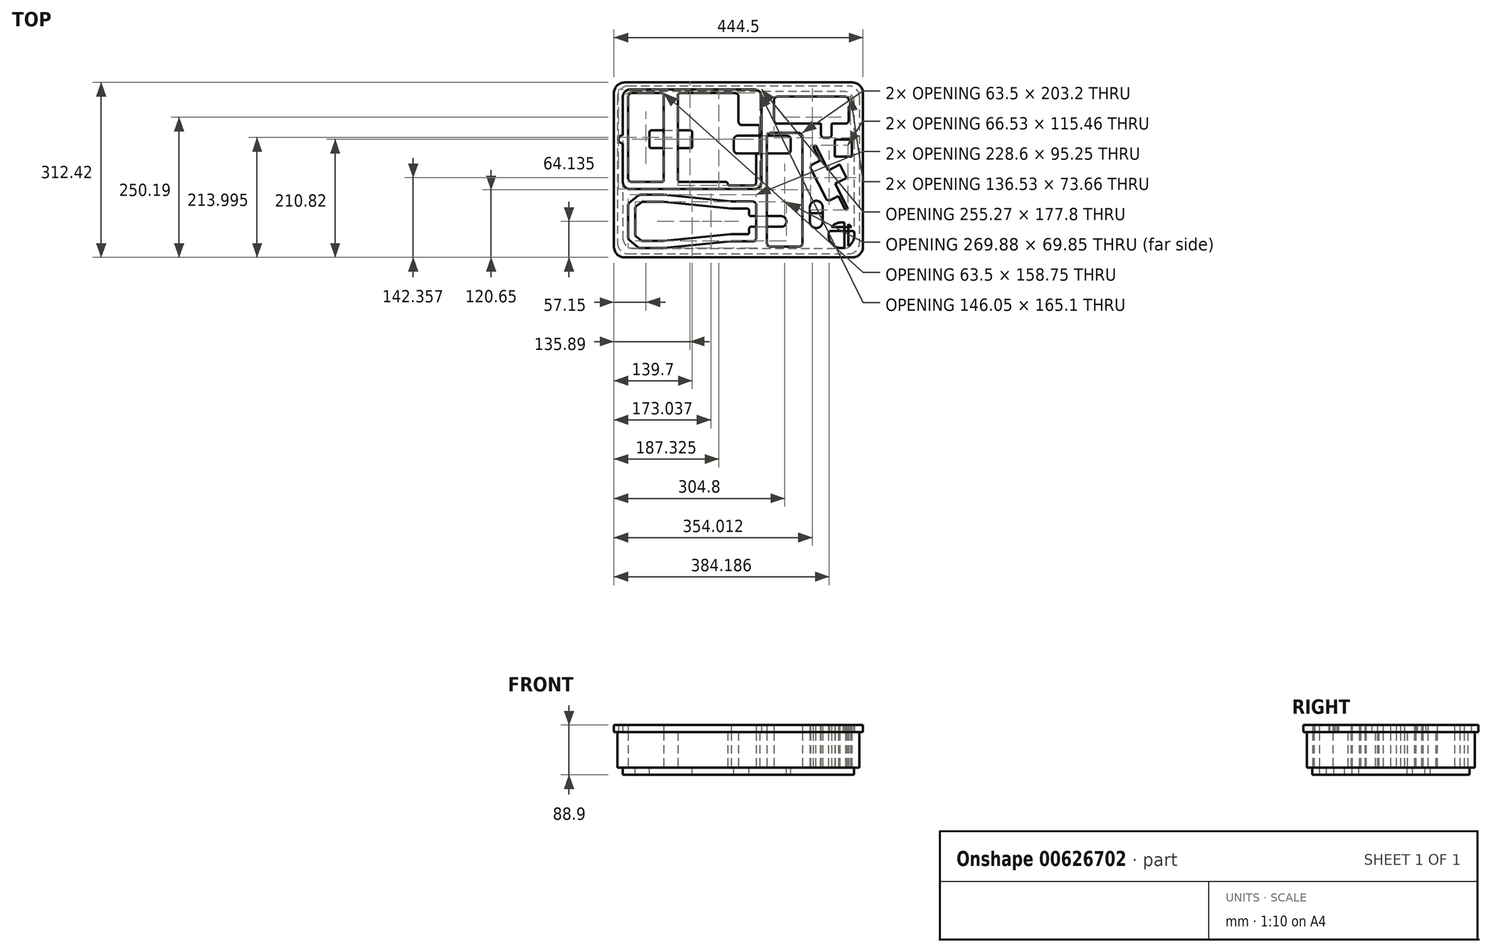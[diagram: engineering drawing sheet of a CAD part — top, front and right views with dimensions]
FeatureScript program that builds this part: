
annotation { "Feature Type Name" : "Feature", "Feature Type Description" : "" }
export const myFeature = defineFeature(function(context is Context, id is Id, definition is map)
    precondition{}
    {
        {
            var Q0;
            Q0=qCreatedBy(makeId("Top.planeOp"),FACE);
            var sketch = newSketch(context, id + "F0", { "sketchPlane" : qUnion([Q0])});
            skLineSegment(sketch, "E0.bottom", {"start": v(-196.85, 149.86) * mm, "end": v(196.85, 149.86) * mm});
            skLineSegment(sketch, "E0.top", {"start": v(-196.85, -149.86) * mm, "end": v(196.85, -149.86) * mm});
            skLineSegment(sketch, "E0.left", {"start": v(-215.9, 130.81) * mm, "end": v(-215.9, -130.81) * mm});
            skLineSegment(sketch, "E0.right", {"start": v(215.9, 130.81) * mm, "end": v(215.9, -130.8) * mm});
            skLineSegment(sketch, "E1.bottom", {"start": v(-196.85, -15.24) * mm, "end": v(-196.85, 130.81) * mm});
            skLineSegment(sketch, "E1.top", {"start": v(31.75, -21.59) * mm, "end": v(31.75, 26.04) * mm});
            skLineSegment(sketch, "E1.right", {"start": v(-190.5, 137.16) * mm, "end": v(-136.52, 137.16) * mm});
            skLineSegment(sketch, "E2.bottom", {"start": v(171.94, 54.19) * mm, "end": v(202.42, 54.19) * mm});
            skLineSegment(sketch, "E2.top", {"start": v(171.94, 23.7) * mm, "end": v(202.42, 23.7) * mm});
            skLineSegment(sketch, "E2.left", {"start": v(171.94, 54.19) * mm, "end": v(171.94, 23.7) * mm});
            skLineSegment(sketch, "E2.right", {"start": v(202.42, 54.19) * mm, "end": v(202.42, 23.7) * mm});
            skLineSegment(sketch, "E3", {"start": v(142.6, -24.8) * mm, "end": v(186.74, -2.32) * mm, "construction": true});
            skLineSegment(sketch, "E4", {"start": v(142.6, -24.8) * mm, "end": v(155.87, -50.83) * mm});
            skLineSegment(sketch, "E5", {"start": v(164.4, -53.6) * mm, "end": v(177.99, -46.7) * mm});
            skLineSegment(sketch, "E6", {"start": v(177.99, -46.7) * mm, "end": v(190.67, -71.59) * mm});
            skLineSegment(sketch, "E7", {"start": v(190.67, -71.59) * mm, "end": v(195.2, -69.28) * mm});
            skLineSegment(sketch, "E8", {"start": v(160.32, -0.82) * mm, "end": v(180.68, 9.56) * mm});
            skLineSegment(sketch, "E9", {"start": v(180.68, 9.56) * mm, "end": v(186.74, -2.32) * mm});
            skPoint(sketch, "E10.visualSharp", {"position": v(158.75, -56.5) * mm});
            skArc(sketch, "E10.filletArc", {"start": v(155.87, -50.83) * mm, "mid": v(159.56, -54) * mm, "end": v(164.4, -53.6) * mm});
            skArc(sketch, "E11.MirrorCS", {"start": v(129.35, 1.22) * mm, "mid": v(128.96, 6.06) * mm, "end": v(132.12, 9.76) * mm});
            skLineSegment(sketch, "E12.MirrorCS", {"start": v(145.7, 16.68) * mm, "end": v(133.02, 41.57) * mm});
            skLineSegment(sketch, "E13.MirrorCS", {"start": v(132.12, 9.76) * mm, "end": v(145.7, 16.68) * mm});
            skPoint(sketch, "E14.MirrorP", {"position": v(126.46, 6.88) * mm});
            skLineSegment(sketch, "E15.MirrorCS", {"start": v(172.42, -24.58) * mm, "end": v(192.8, -14.2) * mm});
            skLineSegment(sketch, "E16.MirrorCS", {"start": v(142.6, -24.8) * mm, "end": v(129.35, 1.22) * mm});
            skLineSegment(sketch, "E17.MirrorCS", {"start": v(192.8, -14.2) * mm, "end": v(186.74, -2.32) * mm});
            skLineSegment(sketch, "E18", {"start": v(172.42, -24.58) * mm, "end": v(195.2, -69.28) * mm});
            skPoint(sketch, "E19.visualSharp", {"position": v(-215.9, 149.86) * mm});
            skArc(sketch, "E19.filletArc", {"start": v(-196.85, 149.86) * mm, "mid": v(-210.32, 144.28) * mm, "end": v(-215.9, 130.81) * mm});
            skPoint(sketch, "E20.visualSharp", {"position": v(215.9, 149.86) * mm});
            skArc(sketch, "E20.filletArc", {"start": v(215.9, 130.81) * mm, "mid": v(210.32, 144.28) * mm, "end": v(196.85, 149.86) * mm});
            skPoint(sketch, "E21.visualSharp", {"position": v(215.9, -149.86) * mm});
            skArc(sketch, "E21.filletArc", {"start": v(196.85, -149.86) * mm, "mid": v(210.32, -144.28) * mm, "end": v(215.9, -130.8) * mm});
            skPoint(sketch, "E22.visualSharp", {"position": v(-215.9, -149.86) * mm});
            skArc(sketch, "E22.filletArc", {"start": v(-215.9, -130.81) * mm, "mid": v(-210.32, -144.28) * mm, "end": v(-196.85, -149.86) * mm});
            skPoint(sketch, "E23.visualSharp", {"position": v(-196.85, -27.94) * mm});
            skPoint(sketch, "E24.visualSharp", {"position": v(31.75, -27.94) * mm});
            skArc(sketch, "E24.filletArc", {"start": v(25.4, -27.94) * mm, "mid": v(29.9, -26.08) * mm, "end": v(31.75, -21.59) * mm});
            skPoint(sketch, "E25.visualSharp", {"position": v(-196.85, 137.16) * mm});
            skArc(sketch, "E25.filletArc", {"start": v(-190.5, 137.16) * mm, "mid": v(-195, 135.3) * mm, "end": v(-196.85, 130.81) * mm});
            skPoint(sketch, "E26.visualSharp", {"position": v(31.75, 137.16) * mm});
            skArc(sketch, "E26.filletArc", {"start": v(31.75, 130.81) * mm, "mid": v(29.9, 135.3) * mm, "end": v(25.4, 137.16) * mm, "construction": true});
            skLineSegment(sketch, "E27.bottom", {"start": v(63.5, 88.9) * mm, "end": v(63.5, 124.46) * mm});
            skLineSegment(sketch, "E27.top", {"start": v(196.85, 88.9) * mm, "end": v(196.85, 112.08) * mm});
            skLineSegment(sketch, "E27.left", {"start": v(69.85, 82.55) * mm, "end": v(146.05, 82.55) * mm});
            skLineSegment(sketch, "E27.right", {"start": v(69.85, 130.81) * mm, "end": v(190.5, 130.81) * mm});
            skLineSegment(sketch, "E28.bottom", {"start": v(147.32, 81.28) * mm, "end": v(147.32, 63.5) * mm});
            skLineSegment(sketch, "E28.top", {"start": v(166.37, 81.28) * mm, "end": v(166.37, 63.5) * mm});
            skLineSegment(sketch, "E28.right", {"start": v(153.67, 57.15) * mm, "end": v(160.02, 57.15) * mm});
            skLineSegment(sketch, "E29.trimOffspring", {"start": v(167.64, 82.55) * mm, "end": v(190.5, 82.55) * mm});
            skLineSegment(sketch, "E30", {"start": v(147.32, 82.55) * mm, "end": v(166.37, 82.55) * mm, "construction": true});
            skPoint(sketch, "E31.visualSharp", {"position": v(63.5, 82.55) * mm});
            skArc(sketch, "E31.filletArc", {"start": v(63.5, 88.9) * mm, "mid": v(65.36, 84.4) * mm, "end": v(69.85, 82.55) * mm});
            skPoint(sketch, "E32.visualSharp", {"position": v(196.85, 82.55) * mm});
            skArc(sketch, "E32.filletArc", {"start": v(190.5, 82.55) * mm, "mid": v(195, 84.4) * mm, "end": v(196.85, 88.9) * mm});
            skArc(sketch, "E33.filletArc", {"start": v(196.85, 124.46) * mm, "mid": v(195, 128.95) * mm, "end": v(190.5, 130.81) * mm});
            skPoint(sketch, "E34.visualSharp", {"position": v(63.5, 130.81) * mm});
            skArc(sketch, "E34.filletArc", {"start": v(69.85, 130.81) * mm, "mid": v(65.36, 128.95) * mm, "end": v(63.5, 124.46) * mm});
            skPoint(sketch, "E35.visualSharp", {"position": v(147.32, 57.15) * mm});
            skArc(sketch, "E35.filletArc", {"start": v(147.32, 63.5) * mm, "mid": v(149.18, 59) * mm, "end": v(153.67, 57.15) * mm});
            skPoint(sketch, "E36.visualSharp", {"position": v(166.37, 57.15) * mm});
            skArc(sketch, "E36.filletArc", {"start": v(160.02, 57.15) * mm, "mid": v(164.51, 59) * mm, "end": v(166.37, 63.5) * mm});
            skLineSegment(sketch, "E37.bottom", {"start": v(127.38, -76.93) * mm, "end": v(150.49, -76.93) * mm});
            skLineSegment(sketch, "E37.left", {"start": v(127.38, -76.93) * mm, "end": v(127.38, -92.17) * mm});
            skLineSegment(sketch, "E37.right", {"start": v(150.49, -76.93) * mm, "end": v(150.49, -92.17) * mm});
            skArc(sketch, "E38", {"start": v(127.38, -92.17) * mm, "mid": v(138.93, -103.73) * mm, "end": v(150.49, -92.17) * mm});
            skLineSegment(sketch, "E39.bottom", {"start": v(-196.85, -139.7) * mm, "end": v(-196.85, -44.45) * mm, "construction": true});
            skLineSegment(sketch, "E39.top", {"start": v(31.75, -139.7) * mm, "end": v(31.75, -44.45) * mm, "construction": true});
            skLineSegment(sketch, "E39.left", {"start": v(-196.85, -139.7) * mm, "end": v(31.75, -139.7) * mm, "construction": true});
            skLineSegment(sketch, "E39.right", {"start": v(-196.85, -44.45) * mm, "end": v(31.75, -44.45) * mm, "construction": true});
            skLineSegment(sketch, "E40", {"start": v(-196.85, -92.08) * mm, "end": v(31.75, -92.07) * mm, "construction": true});
            skLineSegment(sketch, "E41", {"start": v(-196.85, -123.83) * mm, "end": v(31.75, -123.82) * mm, "construction": true});
            skLineSegment(sketch, "E42.MirrorCS", {"start": v(-196.85, -60.33) * mm, "end": v(31.75, -60.32) * mm, "construction": true});
            skLineSegment(sketch, "E43", {"start": v(-196.85, -127.64) * mm, "end": v(31.75, -127.63) * mm, "construction": true});
            skLineSegment(sketch, "E44.MirrorCS", {"start": v(-196.85, -56.51) * mm, "end": v(31.75, -56.51) * mm, "construction": true});
            skLineSegment(sketch, "E45", {"start": v(-177.16, -139.7) * mm, "end": v(-177.16, -44.45) * mm, "construction": true});
            skLineSegment(sketch, "E46", {"start": v(-133.35, -139.7) * mm, "end": v(-133.35, -44.45) * mm, "construction": true});
            skLineSegment(sketch, "E47", {"start": v(-12.7, -139.7) * mm, "end": v(-12.7, -44.45) * mm, "construction": true});
            skLineSegment(sketch, "E48", {"start": v(-196.85, -120.79) * mm, "end": v(-196.85, -63.36) * mm});
            skLineSegment(sketch, "E49", {"start": v(-194.49, -58.42) * mm, "end": v(-178.9, -45.86) * mm});
            skLineSegment(sketch, "E50", {"start": v(-174.92, -44.45) * mm, "end": v(-133.35, -44.45) * mm});
            skLineSegment(sketch, "E51", {"start": v(-133.35, -44.45) * mm, "end": v(-12.7, -56.51) * mm});
            skLineSegment(sketch, "E52", {"start": v(-12.7, -56.51) * mm, "end": v(25.4, -56.51) * mm});
            skLineSegment(sketch, "E53", {"start": v(31.75, -62.86) * mm, "end": v(31.75, -121.28) * mm});
            skLineSegment(sketch, "E54", {"start": v(25.4, -127.63) * mm, "end": v(-12.7, -127.63) * mm});
            skLineSegment(sketch, "E55", {"start": v(-12.7, -127.64) * mm, "end": v(-133.35, -139.7) * mm});
            skLineSegment(sketch, "E56", {"start": v(-133.35, -139.7) * mm, "end": v(-174.92, -139.7) * mm});
            skLineSegment(sketch, "E57", {"start": v(-178.9, -138.3) * mm, "end": v(-194.49, -125.73) * mm});
            skPoint(sketch, "E58.visualSharp", {"position": v(31.75, -127.64) * mm});
            skArc(sketch, "E58.filletArc", {"start": v(25.4, -127.63) * mm, "mid": v(29.9, -125.78) * mm, "end": v(31.75, -121.28) * mm});
            skPoint(sketch, "E59.visualSharp", {"position": v(31.75, -56.51) * mm});
            skArc(sketch, "E59.filletArc", {"start": v(31.75, -62.86) * mm, "mid": v(29.9, -58.37) * mm, "end": v(25.4, -56.51) * mm});
            skPoint(sketch, "E60.visualSharp", {"position": v(-196.85, -123.83) * mm});
            skArc(sketch, "E60.filletArc", {"start": v(-196.85, -120.79) * mm, "mid": v(-196.23, -123.53) * mm, "end": v(-194.49, -125.73) * mm});
            skPoint(sketch, "E61.visualSharp", {"position": v(-177.16, -139.7) * mm});
            skArc(sketch, "E61.filletArc", {"start": v(-178.9, -138.3) * mm, "mid": v(-177.04, -139.34) * mm, "end": v(-174.92, -139.7) * mm});
            skPoint(sketch, "E62.visualSharp", {"position": v(-196.85, -60.33) * mm});
            skArc(sketch, "E62.filletArc", {"start": v(-194.49, -58.42) * mm, "mid": v(-196.23, -60.62) * mm, "end": v(-196.85, -63.36) * mm});
            skPoint(sketch, "E63.visualSharp", {"position": v(-177.16, -44.45) * mm});
            skArc(sketch, "E63.filletArc", {"start": v(-174.92, -44.45) * mm, "mid": v(-177.04, -44.81) * mm, "end": v(-178.9, -45.86) * mm});
            skLineSegment(sketch, "E64", {"start": v(127.38, -92.17) * mm, "end": v(150.49, -92.17) * mm, "construction": true});
            skLineSegment(sketch, "E65.MirrorCS", {"start": v(160.32, -0.82) * mm, "end": v(137.54, 43.88) * mm});
            skLineSegment(sketch, "E66.MirrorCS", {"start": v(133.02, 41.57) * mm, "end": v(137.54, 43.88) * mm});
            skLineSegment(sketch, "E67", {"start": v(198.12, 122.87) * mm, "end": v(198.76, 122.87) * mm});
            skLineSegment(sketch, "E68", {"start": v(200.02, 121.6) * mm, "end": v(200.02, 114.62) * mm});
            skLineSegment(sketch, "E69", {"start": v(198.76, 113.35) * mm, "end": v(198.12, 113.35) * mm});
            skPoint(sketch, "E70.visualSharp", {"position": v(166.37, 82.55) * mm});
            skArc(sketch, "E70.filletArc", {"start": v(167.64, 82.55) * mm, "mid": v(166.74, 82.18) * mm, "end": v(166.37, 81.28) * mm});
            skPoint(sketch, "E71.visualSharp", {"position": v(147.32, 82.55) * mm});
            skArc(sketch, "E71.filletArc", {"start": v(147.32, 81.28) * mm, "mid": v(146.95, 82.18) * mm, "end": v(146.05, 82.55) * mm});
            skPoint(sketch, "E72.visualSharp", {"position": v(200.03, 113.35) * mm});
            skArc(sketch, "E72.filletArc", {"start": v(198.76, 113.35) * mm, "mid": v(199.65, 113.72) * mm, "end": v(200.03, 114.62) * mm});
            skPoint(sketch, "E73.visualSharp", {"position": v(200.03, 122.87) * mm});
            skArc(sketch, "E73.filletArc", {"start": v(200.02, 121.6) * mm, "mid": v(199.65, 122.5) * mm, "end": v(198.76, 122.87) * mm});
            skPoint(sketch, "E74.visualSharp", {"position": v(196.85, 122.87) * mm});
            skArc(sketch, "E74.filletArc", {"start": v(196.85, 124.13) * mm, "mid": v(197.23, 123.24) * mm, "end": v(198.12, 122.87) * mm});
            skPoint(sketch, "E75.visualSharp", {"position": v(196.85, 113.35) * mm});
            skArc(sketch, "E75.filletArc", {"start": v(198.12, 113.35) * mm, "mid": v(197.22, 112.98) * mm, "end": v(196.85, 112.08) * mm});
            skLineSegment(sketch, "E76", {"start": v(-196.85, 54.61) * mm, "end": v(31.75, 54.61) * mm, "construction": true});
            skLineSegment(sketch, "E77", {"start": v(-82.55, -27.94) * mm, "end": v(-82.55, 137.16) * mm, "construction": true});
            skLineSegment(sketch, "E78", {"start": v(0, 149.86) * mm, "end": v(0, -149.86) * mm, "construction": true});
            skLineSegment(sketch, "E79", {"start": v(-215.9, 0) * mm, "end": v(215.9, 0) * mm, "construction": true});
            skPoint(sketch, "E80", {"position": v(0, 0) * mm});
            skPoint(sketch, "E81", {"position": v(-82.55, 54.61) * mm});
            skPoint(sketch, "E82", {"position": v(-133.35, -92.08) * mm});
            skLineSegment(sketch, "E83", {"start": v(63.5, 106.68) * mm, "end": v(196.85, 106.68) * mm, "construction": true});
            skLineSegment(sketch, "E84", {"start": v(130.18, 130.81) * mm, "end": v(130.18, 82.55) * mm, "construction": true});
            skPoint(sketch, "E85", {"position": v(130.18, 106.68) * mm});
            skLineSegment(sketch, "E86", {"start": v(172.42, -24.58) * mm, "end": v(160.32, -0.82) * mm, "construction": true});
            skPoint(sketch, "E87", {"position": v(166.37, -12.7) * mm});
            skLineSegment(sketch, "E88", {"start": v(196.85, 124.46) * mm, "end": v(196.85, 124.13) * mm});
            skLineSegment(sketch, "E89", {"start": v(196.85, 124.13) * mm, "end": v(196.85, 112.08) * mm, "construction": true});
            skArc(sketch, "E90", {"start": v(31.75, -21.59) * mm, "mid": v(29.9, -26.08) * mm, "end": v(25.4, -27.94) * mm});
            skLineSegment(sketch, "E91.bottom", {"start": v(107.95, -137.16) * mm, "end": v(57.15, -137.16) * mm});
            skLineSegment(sketch, "E91.top", {"start": v(107.95, 66.04) * mm, "end": v(57.15, 66.04) * mm});
            skLineSegment(sketch, "E91.left", {"start": v(114.3, -130.8) * mm, "end": v(114.3, 59.7) * mm});
            skLineSegment(sketch, "E91.right", {"start": v(50.8, -130.8) * mm, "end": v(50.8, 59.7) * mm});
            skLineSegment(sketch, "E92", {"start": v(82.55, -137.16) * mm, "end": v(82.55, 66.04) * mm, "construction": true});
            skLineSegment(sketch, "E93", {"start": v(114.3, -35.56) * mm, "end": v(50.8, -35.56) * mm, "construction": true});
            skPoint(sketch, "E94", {"position": v(82.55, -35.56) * mm});
            skPoint(sketch, "E95.visualSharp", {"position": v(114.3, -137.16) * mm});
            skArc(sketch, "E95.filletArc", {"start": v(107.95, -137.16) * mm, "mid": v(112.44, -135.3) * mm, "end": v(114.3, -130.8) * mm});
            skPoint(sketch, "E96.visualSharp", {"position": v(50.8, -137.16) * mm});
            skArc(sketch, "E96.filletArc", {"start": v(50.8, -130.8) * mm, "mid": v(52.66, -135.3) * mm, "end": v(57.15, -137.16) * mm});
            skPoint(sketch, "E97.visualSharp", {"position": v(50.8, 66.04) * mm});
            skArc(sketch, "E97.filletArc", {"start": v(57.15, 66.04) * mm, "mid": v(52.66, 64.18) * mm, "end": v(50.8, 59.7) * mm});
            skPoint(sketch, "E98.visualSharp", {"position": v(114.3, 66.04) * mm});
            skArc(sketch, "E98.filletArc", {"start": v(114.3, 59.7) * mm, "mid": v(112.44, 64.18) * mm, "end": v(107.95, 66.04) * mm});
            skLineSegment(sketch, "E99.left", {"start": v(-107.95, 133.99) * mm, "end": v(-107.95, -18.41) * mm});
            skLineSegment(sketch, "E99.right", {"start": v(-133.35, 133.99) * mm, "end": v(-133.35, -18.41) * mm});
            skLineSegment(sketch, "E100", {"start": v(34.93, 80.01) * mm, "end": v(34.92, 80.01) * mm});
            skLineSegment(sketch, "E101.MirrorCS", {"start": v(34.93, 29.21) * mm, "end": v(34.93, 29.21) * mm});
            skLineSegment(sketch, "E102", {"start": v(38.1, 76.84) * mm, "end": v(38.1, 32.39) * mm});
            skLineSegment(sketch, "E103", {"start": v(-104.78, 137.16) * mm, "end": v(-6.35, 137.16) * mm});
            skLineSegment(sketch, "E104", {"start": v(31.75, 83.19) * mm, "end": v(31.75, 130.81) * mm, "construction": true});
            skLineSegment(sketch, "E105", {"start": v(31.75, 29.21) * mm, "end": v(31.75, 80.01) * mm, "construction": true});
            skLineSegment(sketch, "E106", {"start": v(-133.35, 137.16) * mm, "end": v(-107.95, 137.16) * mm, "construction": true});
            skPoint(sketch, "E107.visualSharp", {"position": v(-107.95, 137.16) * mm});
            skArc(sketch, "E107.filletArc", {"start": v(-104.78, 137.16) * mm, "mid": v(-107.02, 136.23) * mm, "end": v(-107.95, 133.99) * mm});
            skPoint(sketch, "E108.visualSharp", {"position": v(-133.35, 137.16) * mm});
            skArc(sketch, "E108.filletArc", {"start": v(-133.35, 133.99) * mm, "mid": v(-134.28, 136.23) * mm, "end": v(-136.52, 137.16) * mm});
            skPoint(sketch, "E109.visualSharp", {"position": v(31.75, 80.01) * mm});
            skPoint(sketch, "E110.visualSharp", {"position": v(31.75, 29.21) * mm});
            skArc(sketch, "E110.filletArc", {"start": v(34.93, 29.21) * mm, "mid": v(32.68, 28.28) * mm, "end": v(31.75, 26.04) * mm});
            skPoint(sketch, "E111.visualSharp", {"position": v(38.1, 29.21) * mm});
            skArc(sketch, "E111.filletArc", {"start": v(34.93, 29.21) * mm, "mid": v(37.17, 30.14) * mm, "end": v(38.1, 32.39) * mm});
            skPoint(sketch, "E112.visualSharp", {"position": v(38.1, 80.01) * mm});
            skArc(sketch, "E112.filletArc", {"start": v(38.1, 76.84) * mm, "mid": v(37.17, 79.08) * mm, "end": v(34.92, 80.01) * mm});
            skLineSegment(sketch, "E113", {"start": v(0, 130.81) * mm, "end": v(0, 86.36) * mm});
            skLineSegment(sketch, "E114", {"start": v(6.35, 80.01) * mm, "end": v(34.93, 80.01) * mm});
            skPoint(sketch, "E115.visualSharp", {"position": v(0, 80.01) * mm});
            skArc(sketch, "E115.filletArc", {"start": v(0, 86.36) * mm, "mid": v(1.86, 81.87) * mm, "end": v(6.35, 80.01) * mm});
            skLineSegment(sketch, "E116", {"start": v(-6.35, 137.16) * mm, "end": v(0, 137.16) * mm, "construction": true});
            skLineSegment(sketch, "E117", {"start": v(0, 137.16) * mm, "end": v(25.4, 137.16) * mm, "construction": true});
            skPoint(sketch, "E118.visualSharp", {"position": v(0, 137.16) * mm});
            skArc(sketch, "E118.filletArc", {"start": v(0, 130.81) * mm, "mid": v(-1.86, 135.3) * mm, "end": v(-6.35, 137.16) * mm});
            skLineSegment(sketch, "E119", {"start": v(-6.35, 137.16) * mm, "end": v(-6.35, 137.16) * mm});
            skLineSegment(sketch, "E120", {"start": v(-19.05, -24.76) * mm, "end": v(-19.05, -24.76) * mm});
            skLineSegment(sketch, "E121", {"start": v(-22.22, -21.59) * mm, "end": v(-104.78, -21.59) * mm});
            skLineSegment(sketch, "E122", {"start": v(-133.35, -21.59) * mm, "end": v(-133.35, -24.76) * mm, "construction": true});
            skLineSegment(sketch, "E123", {"start": v(-15.88, -27.94) * mm, "end": v(25.4, -27.94) * mm});
            skLineSegment(sketch, "E124", {"start": v(-107.95, -21.59) * mm, "end": v(-107.95, -24.76) * mm, "construction": true});
            skPoint(sketch, "E125.visualSharp", {"position": v(-196.85, -21.59) * mm});
            skArc(sketch, "E125.filletArc", {"start": v(-196.85, -15.24) * mm, "mid": v(-195, -19.73) * mm, "end": v(-190.5, -21.59) * mm});
            skPoint(sketch, "E126.visualSharp", {"position": v(-19.05, -21.59) * mm});
            skArc(sketch, "E126.filletArc", {"start": v(-19.05, -24.76) * mm, "mid": v(-19.98, -22.52) * mm, "end": v(-22.22, -21.59) * mm});
            skPoint(sketch, "E127.visualSharp", {"position": v(-19.05, -27.94) * mm});
            skArc(sketch, "E127.filletArc", {"start": v(-19.05, -24.76) * mm, "mid": v(-18.12, -27.01) * mm, "end": v(-15.88, -27.94) * mm});
            skLineSegment(sketch, "E128", {"start": v(-136.53, -21.59) * mm, "end": v(-190.5, -21.59) * mm});
            skPoint(sketch, "E129.visualSharp", {"position": v(-133.35, -21.59) * mm});
            skArc(sketch, "E129.filletArc", {"start": v(-136.53, -21.59) * mm, "mid": v(-134.28, -20.66) * mm, "end": v(-133.35, -18.41) * mm});
            skPoint(sketch, "E130.visualSharp", {"position": v(-107.95, -21.59) * mm});
            skArc(sketch, "E130.filletArc", {"start": v(-107.95, -18.41) * mm, "mid": v(-107.02, -20.66) * mm, "end": v(-104.78, -21.59) * mm});
            skSolve(sketch);
        }
        {
            var Q0;
            Q0=qSketchRegion(id+"F0",true);
            extrude(context, id + "F1", {"entities" : qUnion([Q0]), "depth" : 63.5 * mm, "offsetDistance" : 25.4 * mm});
        }
        {
            var Q0;
            Q0=qCreatedBy(makeId("Top.planeOp"),FACE);
            var sketch = newSketch(context, id + "F2", { "sketchPlane" : qUnion([Q0])});
            skLineSegment(sketch, "E131.0", {"start": v(-215.9, 149.86) * mm, "end": v(215.9, 149.86) * mm, "construction": true});
            skLineSegment(sketch, "E132.0", {"start": v(-215.9, 149.86) * mm, "end": v(-215.9, -149.86) * mm, "construction": true});
            skLineSegment(sketch, "E133.0", {"start": v(215.9, 149.86) * mm, "end": v(215.9, -149.86) * mm, "construction": true});
            skLineSegment(sketch, "E134.0", {"start": v(-190.26, -149.86) * mm, "end": v(215.9, -149.86) * mm, "construction": true});
            skPoint(sketch, "E135.orphan", {"position": v(-196.85, 149.86) * mm});
            skPoint(sketch, "E136.orphan", {"position": v(-215.9, 130.81) * mm});
            skPoint(sketch, "E137.orphan", {"position": v(196.85, 149.86) * mm});
            skPoint(sketch, "E138.orphan", {"position": v(215.9, 130.81) * mm});
            skPoint(sketch, "E139.orphan", {"position": v(215.9, -130.8) * mm});
            skPoint(sketch, "E140.orphan", {"position": v(196.85, -149.86) * mm});
            skPoint(sketch, "E141.orphan", {"position": v(-196.85, -149.86) * mm});
            skPoint(sketch, "E142.orphan", {"position": v(-215.9, -130.81) * mm});
            skPoint(sketch, "E143", {"position": v(0, 0) * mm});
            skLineSegment(sketch, "E144", {"start": v(0, 149.86) * mm, "end": v(0, -149.86) * mm, "construction": true});
            skPoint(sketch, "E144.startSnap0", {"position": v(0, 149.86) * mm});
            skLineSegment(sketch, "E145", {"start": v(-215.9, 0) * mm, "end": v(215.9, 0) * mm, "construction": true});
            skLineSegment(sketch, "E146.bottom", {"start": v(-187.32, 140.34) * mm, "end": v(187.33, 140.34) * mm});
            skLineSegment(sketch, "E146.top", {"start": v(-187.33, -140.33) * mm, "end": v(187.32, -140.33) * mm});
            skLineSegment(sketch, "E146.left", {"start": v(-206.38, 121.29) * mm, "end": v(-206.38, -121.28) * mm});
            skLineSegment(sketch, "E146.right", {"start": v(206.38, 121.29) * mm, "end": v(206.38, -121.28) * mm});
            skPoint(sketch, "E147.visualSharp", {"position": v(-206.38, 140.34) * mm});
            skPoint(sketch, "E148.visualSharp", {"position": v(206.38, 140.34) * mm});
            skPoint(sketch, "E149.visualSharp", {"position": v(206.38, -140.33) * mm});
            skPoint(sketch, "E150.visualSharp", {"position": v(-206.38, -140.33) * mm});
            skLineSegment(sketch, "E151.0.0", {"start": v(-12.7, -127.63) * mm, "end": v(25.4, -127.63) * mm, "construction": true});
            skArc(sketch, "E151.0.1", {"start": v(25.4, -127.63) * mm, "mid": v(29.9, -125.78) * mm, "end": v(31.75, -121.28) * mm, "construction": true});
            skLineSegment(sketch, "E151.0.2", {"start": v(31.75, -121.28) * mm, "end": v(31.75, -62.86) * mm, "construction": true});
            skArc(sketch, "E151.0.3", {"start": v(31.75, -62.86) * mm, "mid": v(29.9, -58.37) * mm, "end": v(25.4, -56.51) * mm, "construction": true});
            skLineSegment(sketch, "E151.0.4", {"start": v(25.4, -56.51) * mm, "end": v(-12.7, -56.51) * mm, "construction": true});
            skLineSegment(sketch, "E151.0.5", {"start": v(-12.7, -56.52) * mm, "end": v(-133.35, -44.45) * mm, "construction": true});
            skLineSegment(sketch, "E151.0.6", {"start": v(-133.35, -44.45) * mm, "end": v(-174.92, -44.45) * mm, "construction": true});
            skArc(sketch, "E151.0.7", {"start": v(-174.92, -44.45) * mm, "mid": v(-177.04, -44.81) * mm, "end": v(-178.9, -45.86) * mm, "construction": true});
            skLineSegment(sketch, "E151.0.8", {"start": v(-178.9, -45.86) * mm, "end": v(-194.49, -58.42) * mm, "construction": true});
            skArc(sketch, "E151.0.9", {"start": v(-194.49, -58.42) * mm, "mid": v(-196.23, -60.62) * mm, "end": v(-196.85, -63.36) * mm, "construction": true});
            skLineSegment(sketch, "E151.0.10", {"start": v(-196.85, -63.36) * mm, "end": v(-196.85, -120.79) * mm, "construction": true});
            skArc(sketch, "E151.0.11", {"start": v(-196.85, -120.79) * mm, "mid": v(-196.23, -123.53) * mm, "end": v(-194.49, -125.73) * mm, "construction": true});
            skLineSegment(sketch, "E151.0.12", {"start": v(-194.49, -125.73) * mm, "end": v(-178.9, -138.3) * mm, "construction": true});
            skArc(sketch, "E151.0.13", {"start": v(-178.9, -138.3) * mm, "mid": v(-177.04, -139.34) * mm, "end": v(-174.92, -139.7) * mm, "construction": true});
            skLineSegment(sketch, "E151.0.14", {"start": v(-174.92, -139.7) * mm, "end": v(-133.35, -139.7) * mm, "construction": true});
            skLineSegment(sketch, "E151.0.15", {"start": v(-133.35, -139.7) * mm, "end": v(-12.7, -127.64) * mm, "construction": true});
            skArc(sketch, "E152.filletArc", {"start": v(-187.32, 140.34) * mm, "mid": v(-200.8, 134.76) * mm, "end": v(-206.38, 121.29) * mm});
            skArc(sketch, "E153.filletArc", {"start": v(206.38, 121.29) * mm, "mid": v(200.8, 134.76) * mm, "end": v(187.33, 140.34) * mm});
            skArc(sketch, "E154.filletArc", {"start": v(187.32, -140.33) * mm, "mid": v(200.8, -134.76) * mm, "end": v(206.37, -121.28) * mm});
            skArc(sketch, "E155.filletArc", {"start": v(-206.38, -121.28) * mm, "mid": v(-200.8, -134.76) * mm, "end": v(-187.33, -140.33) * mm});
            skLineSegment(sketch, "E156.0", {"start": v(-173.55, -57.85) * mm, "end": v(-182.97, -65.45) * mm});
            skLineSegment(sketch, "E156.1", {"start": v(-134.14, -57.15) * mm, "end": v(-171.56, -57.15) * mm});
            skLineSegment(sketch, "E156.2", {"start": v(-184.15, -67.92) * mm, "end": v(-184.15, -116.23) * mm});
            skLineSegment(sketch, "E156.3", {"start": v(-13.5, -69.2) * mm, "end": v(-133.83, -57.17) * mm});
            skLineSegment(sketch, "E156.4", {"start": v(15.88, -69.21) * mm, "end": v(-13.18, -69.21) * mm});
            skLineSegment(sketch, "E156.5", {"start": v(19.05, -111.76) * mm, "end": v(19.05, -104.78) * mm});
            skLineSegment(sketch, "E156.6", {"start": v(-182.97, -118.7) * mm, "end": v(-173.55, -126.3) * mm});
            skLineSegment(sketch, "E156.7", {"start": v(-171.56, -127) * mm, "end": v(-134.14, -127) * mm});
            skLineSegment(sketch, "E156.8", {"start": v(-133.83, -126.98) * mm, "end": v(-13.5, -114.95) * mm});
            skLineSegment(sketch, "E156.9", {"start": v(-13.18, -114.93) * mm, "end": v(15.88, -114.93) * mm});
            skLineSegment(sketch, "E157", {"start": v(22.23, -82.55) * mm, "end": v(76.2, -82.55) * mm});
            skLineSegment(sketch, "E158", {"start": v(-184.15, -92.08) * mm, "end": v(76.2, -92.08) * mm, "construction": true});
            skLineSegment(sketch, "E159", {"start": v(76.2, -82.55) * mm, "end": v(76.2, -92.08) * mm, "construction": true});
            skLineSegment(sketch, "E160.MirrorCS", {"start": v(22.23, -101.6) * mm, "end": v(76.2, -101.6) * mm});
            skLineSegment(sketch, "E161.MirrorCS", {"start": v(76.2, -101.6) * mm, "end": v(76.2, -92.08) * mm, "construction": true});
            skLineSegment(sketch, "E162", {"start": v(19.05, -79.37) * mm, "end": v(19.05, -72.39) * mm});
            skPoint(sketch, "E163.orphan", {"position": v(19.05, -92.08) * mm});
            skArc(sketch, "E164", {"start": v(76.2, -82.55) * mm, "mid": v(85.73, -92.08) * mm, "end": v(76.2, -101.6) * mm});
            skLineSegment(sketch, "E165.bottom", {"start": v(-1.78, 60.96) * mm, "end": v(87.12, 60.96) * mm});
            skLineSegment(sketch, "E165.top", {"start": v(-1.78, 29.21) * mm, "end": v(87.12, 29.21) * mm});
            skLineSegment(sketch, "E165.left", {"start": v(-8.13, 54.61) * mm, "end": v(-8.13, 35.56) * mm});
            skLineSegment(sketch, "E165.right", {"start": v(93.47, 54.61) * mm, "end": v(93.47, 35.56) * mm});
            skPoint(sketch, "E166.visualSharp", {"position": v(-8.13, 60.96) * mm});
            skArc(sketch, "E166.filletArc", {"start": v(-1.78, 60.96) * mm, "mid": v(-6.27, 59.1) * mm, "end": v(-8.13, 54.61) * mm});
            skPoint(sketch, "E167.visualSharp", {"position": v(93.47, 60.96) * mm});
            skArc(sketch, "E167.filletArc", {"start": v(93.47, 54.61) * mm, "mid": v(91.61, 59.1) * mm, "end": v(87.12, 60.96) * mm});
            skPoint(sketch, "E168.visualSharp", {"position": v(93.47, 29.21) * mm});
            skArc(sketch, "E168.filletArc", {"start": v(87.12, 29.21) * mm, "mid": v(91.61, 31.07) * mm, "end": v(93.47, 35.56) * mm});
            skPoint(sketch, "E169.visualSharp", {"position": v(-8.13, 29.21) * mm});
            skArc(sketch, "E169.filletArc", {"start": v(-8.13, 35.56) * mm, "mid": v(-6.27, 31.07) * mm, "end": v(-1.78, 29.21) * mm});
            skPoint(sketch, "E170.visualSharp", {"position": v(19.05, -69.21) * mm});
            skArc(sketch, "E170.filletArc", {"start": v(19.05, -72.39) * mm, "mid": v(18.12, -70.14) * mm, "end": v(15.88, -69.21) * mm});
            skPoint(sketch, "E171.visualSharp", {"position": v(19.05, -82.55) * mm});
            skArc(sketch, "E171.filletArc", {"start": v(19.05, -79.37) * mm, "mid": v(19.98, -81.62) * mm, "end": v(22.23, -82.55) * mm});
            skPoint(sketch, "E172.visualSharp", {"position": v(19.05, -101.6) * mm});
            skArc(sketch, "E172.filletArc", {"start": v(22.23, -101.6) * mm, "mid": v(19.98, -102.53) * mm, "end": v(19.05, -104.78) * mm});
            skPoint(sketch, "E173.visualSharp", {"position": v(19.05, -114.94) * mm});
            skArc(sketch, "E173.filletArc", {"start": v(15.88, -114.94) * mm, "mid": v(18.12, -114) * mm, "end": v(19.05, -111.76) * mm});
            skPoint(sketch, "E174.visualSharp", {"position": v(-184.15, -66.4) * mm});
            skArc(sketch, "E174.filletArc", {"start": v(-182.97, -65.45) * mm, "mid": v(-183.84, -66.55) * mm, "end": v(-184.15, -67.92) * mm});
            skPoint(sketch, "E175.visualSharp", {"position": v(-172.68, -57.15) * mm});
            skArc(sketch, "E175.filletArc", {"start": v(-171.56, -57.15) * mm, "mid": v(-172.62, -57.33) * mm, "end": v(-173.55, -57.85) * mm});
            skPoint(sketch, "E176.visualSharp", {"position": v(-133.98, -57.15) * mm});
            skArc(sketch, "E176.filletArc", {"start": v(-133.83, -57.17) * mm, "mid": v(-133.98, -57.15) * mm, "end": v(-134.14, -57.15) * mm});
            skPoint(sketch, "E177.visualSharp", {"position": v(-184.15, -117.75) * mm});
            skArc(sketch, "E177.filletArc", {"start": v(-184.15, -116.23) * mm, "mid": v(-183.84, -117.6) * mm, "end": v(-182.97, -118.7) * mm});
            skPoint(sketch, "E178.visualSharp", {"position": v(-172.68, -127) * mm});
            skArc(sketch, "E178.filletArc", {"start": v(-173.55, -126.3) * mm, "mid": v(-172.62, -126.82) * mm, "end": v(-171.56, -127) * mm});
            skPoint(sketch, "E179.visualSharp", {"position": v(-133.98, -127) * mm});
            skArc(sketch, "E179.filletArc", {"start": v(-134.14, -127) * mm, "mid": v(-133.98, -127) * mm, "end": v(-133.83, -126.98) * mm});
            skPoint(sketch, "E180.visualSharp", {"position": v(-13.33, -114.93) * mm});
            skArc(sketch, "E180.filletArc", {"start": v(-13.18, -114.93) * mm, "mid": v(-13.33, -114.94) * mm, "end": v(-13.5, -114.95) * mm});
            skPoint(sketch, "E181.visualSharp", {"position": v(-13.33, -69.21) * mm});
            skArc(sketch, "E181.filletArc", {"start": v(-13.5, -69.2) * mm, "mid": v(-13.33, -69.21) * mm, "end": v(-13.18, -69.21) * mm});
            skLineSegment(sketch, "E182.0", {"start": v(-196.85, 54.61) * mm, "end": v(31.75, 54.61) * mm, "construction": true});
            skLineSegment(sketch, "E183.0", {"start": v(-133.35, 133.99) * mm, "end": v(-133.35, -18.41) * mm, "construction": true});
            skLineSegment(sketch, "E184.0", {"start": v(-107.95, 133.99) * mm, "end": v(-107.95, -18.41) * mm, "construction": true});
            skLineSegment(sketch, "E185", {"start": v(-158.75, 54.61) * mm, "end": v(-158.75, 67.31) * mm});
            skLineSegment(sketch, "E186", {"start": v(-155.57, 70.49) * mm, "end": v(-85.72, 70.49) * mm});
            skLineSegment(sketch, "E187", {"start": v(-82.55, 67.31) * mm, "end": v(-82.55, 54.61) * mm});
            skLineSegment(sketch, "E188.MirrorCS", {"start": v(-82.55, 41.91) * mm, "end": v(-82.55, 54.61) * mm});
            skLineSegment(sketch, "E189.MirrorCS", {"start": v(-158.75, 54.61) * mm, "end": v(-158.75, 41.91) * mm});
            skLineSegment(sketch, "E190.MirrorCS", {"start": v(-155.57, 38.74) * mm, "end": v(-85.72, 38.74) * mm});
            skPoint(sketch, "E191.visualSharp", {"position": v(-158.75, 70.49) * mm});
            skArc(sketch, "E191.filletArc", {"start": v(-155.57, 70.49) * mm, "mid": v(-157.82, 69.56) * mm, "end": v(-158.75, 67.31) * mm});
            skPoint(sketch, "E192.visualSharp", {"position": v(-158.75, 38.74) * mm});
            skArc(sketch, "E192.filletArc", {"start": v(-158.75, 41.91) * mm, "mid": v(-157.82, 39.66) * mm, "end": v(-155.57, 38.74) * mm});
            skPoint(sketch, "E193.visualSharp", {"position": v(-82.55, 38.74) * mm});
            skArc(sketch, "E193.filletArc", {"start": v(-85.72, 38.74) * mm, "mid": v(-83.48, 39.66) * mm, "end": v(-82.55, 41.91) * mm});
            skPoint(sketch, "E194.visualSharp", {"position": v(-82.55, 70.49) * mm});
            skArc(sketch, "E194.filletArc", {"start": v(-82.55, 67.31) * mm, "mid": v(-83.48, 69.56) * mm, "end": v(-85.72, 70.49) * mm});
            skSolve(sketch);
        }
        {
            var Q0;
            Q0=qSketchRegion(id+"F2",true);
            extrude(context, id + "F3", {"entities" : qUnion([Q0]), "oppositeDirection" : true, "depth" : 12.7 * mm, "offsetDistance" : 25.4 * mm});
        }
        {
            var Q0;
            Q0=makeQuery(id+"F1.opExtrude","CAP_FACE",FACE,{"disambiguationData":[OSD([sQuery(id+"F0.wireOp",EDGE,"E0.bottom"),sQuery(id+"F0.wireOp",EDGE,"E0.top"),sQuery(id+"F0.wireOp",EDGE,"E0.left"),sQuery(id+"F0.wireOp",EDGE,"E0.right"),sQuery(id+"F0.wireOp",EDGE,"E1.bottom"),sQuery(id+"F0.wireOp",EDGE,"E1.top"),sQuery(id+"F0.wireOp",EDGE,"E1.left"),sQuery(id+"F0.wireOp",EDGE,"E1.right"),sQuery(id+"F0.wireOp",EDGE,"E2.bottom"),sQuery(id+"F0.wireOp",EDGE,"E2.top"),sQuery(id+"F0.wireOp",EDGE,"E2.left"),sQuery(id+"F0.wireOp",EDGE,"E2.right"),sQuery(id+"F0.wireOp",EDGE,"E4"),sQuery(id+"F0.wireOp",EDGE,"E5"),sQuery(id+"F0.wireOp",EDGE,"E6"),sQuery(id+"F0.wireOp",EDGE,"E7"),sQuery(id+"F0.wireOp",EDGE,"E8"),sQuery(id+"F0.wireOp",EDGE,"E9"),sQuery(id+"F0.wireOp",EDGE,"E10.filletArc"),sQuery(id+"F0.wireOp",EDGE,"E11.MirrorCS"),sQuery(id+"F0.wireOp",EDGE,"E12.MirrorCS"),sQuery(id+"F0.wireOp",EDGE,"E13.MirrorCS"),sQuery(id+"F0.wireOp",EDGE,"E15.MirrorCS"),sQuery(id+"F0.wireOp",EDGE,"E16.MirrorCS"),sQuery(id+"F0.wireOp",EDGE,"E17.MirrorCS"),sQuery(id+"F0.wireOp",EDGE,"E18"),sQuery(id+"F0.wireOp",EDGE,"E19.filletArc"),sQuery(id+"F0.wireOp",EDGE,"E20.filletArc"),sQuery(id+"F0.wireOp",EDGE,"E21.filletArc"),sQuery(id+"F0.wireOp",EDGE,"E22.filletArc"),sQuery(id+"F0.wireOp",EDGE,"E23.filletArc"),sQuery(id+"F0.wireOp",EDGE,"E25.filletArc"),sQuery(id+"F0.wireOp",EDGE,"E26.filletArc"),sQuery(id+"F0.wireOp",EDGE,"E27.bottom"),sQuery(id+"F0.wireOp",EDGE,"E27.top"),sQuery(id+"F0.wireOp",EDGE,"E27.left"),sQuery(id+"F0.wireOp",EDGE,"E27.right"),sQuery(id+"F0.wireOp",EDGE,"E28.bottom"),sQuery(id+"F0.wireOp",EDGE,"E28.top"),sQuery(id+"F0.wireOp",EDGE,"E28.right"),sQuery(id+"F0.wireOp",EDGE,"E29.trimOffspring"),sQuery(id+"F0.wireOp",EDGE,"E31.filletArc"),sQuery(id+"F0.wireOp",EDGE,"E32.filletArc"),sQuery(id+"F0.wireOp",EDGE,"E33.filletArc"),sQuery(id+"F0.wireOp",EDGE,"E34.filletArc"),sQuery(id+"F0.wireOp",EDGE,"E35.filletArc"),sQuery(id+"F0.wireOp",EDGE,"E36.filletArc"),sQuery(id+"F0.wireOp",EDGE,"E37.bottom"),sQuery(id+"F0.wireOp",EDGE,"E37.left"),sQuery(id+"F0.wireOp",EDGE,"E37.right"),sQuery(id+"F0.wireOp",EDGE,"E38"),sQuery(id+"F0.wireOp",EDGE,"E48"),sQuery(id+"F0.wireOp",EDGE,"E49"),sQuery(id+"F0.wireOp",EDGE,"E50"),sQuery(id+"F0.wireOp",EDGE,"E51"),sQuery(id+"F0.wireOp",EDGE,"E52"),sQuery(id+"F0.wireOp",EDGE,"E53"),sQuery(id+"F0.wireOp",EDGE,"E54"),sQuery(id+"F0.wireOp",EDGE,"E55"),sQuery(id+"F0.wireOp",EDGE,"E56"),sQuery(id+"F0.wireOp",EDGE,"E57"),sQuery(id+"F0.wireOp",EDGE,"E58.filletArc"),sQuery(id+"F0.wireOp",EDGE,"E59.filletArc"),sQuery(id+"F0.wireOp",EDGE,"E60.filletArc"),sQuery(id+"F0.wireOp",EDGE,"E61.filletArc"),sQuery(id+"F0.wireOp",EDGE,"E62.filletArc"),sQuery(id+"F0.wireOp",EDGE,"E63.filletArc"),sQuery(id+"F0.wireOp",EDGE,"E65.MirrorCS"),sQuery(id+"F0.wireOp",EDGE,"E66.MirrorCS"),sQuery(id+"F0.wireOp",EDGE,"E67"),sQuery(id+"F0.wireOp",EDGE,"E68"),sQuery(id+"F0.wireOp",EDGE,"E69"),sQuery(id+"F0.wireOp",EDGE,"E70.filletArc"),sQuery(id+"F0.wireOp",EDGE,"E71.filletArc"),sQuery(id+"F0.wireOp",EDGE,"E72.filletArc"),sQuery(id+"F0.wireOp",EDGE,"E73.filletArc"),sQuery(id+"F0.wireOp",EDGE,"E74.filletArc"),sQuery(id+"F0.wireOp",EDGE,"E75.filletArc"),sQuery(id+"F0.wireOp",EDGE,"E88"),sQuery(id+"F0.wireOp",EDGE,"E90"),sQuery(id+"F0.wireOp",EDGE,"E91.bottom"),sQuery(id+"F0.wireOp",EDGE,"E91.top"),sQuery(id+"F0.wireOp",EDGE,"E91.left"),sQuery(id+"F0.wireOp",EDGE,"E91.right"),sQuery(id+"F0.wireOp",EDGE,"E95.filletArc"),sQuery(id+"F0.wireOp",EDGE,"E96.filletArc"),sQuery(id+"F0.wireOp",EDGE,"E97.filletArc"),sQuery(id+"F0.wireOp",EDGE,"E98.filletArc")])],"isStart":false});
            var sketch = newSketch(context, id + "F4", { "sketchPlane" : qUnion([Q0])});
            skLineSegment(sketch, "E195.bottom", {"start": v(-203.2, 156.21) * mm, "end": v(203.2, 156.21) * mm});
            skLineSegment(sketch, "E195.top", {"start": v(-203.2, -156.2) * mm, "end": v(203.2, -156.2) * mm});
            skLineSegment(sketch, "E195.left", {"start": v(-222.25, 137.16) * mm, "end": v(-222.25, -137.16) * mm});
            skLineSegment(sketch, "E195.right", {"start": v(222.25, 137.16) * mm, "end": v(222.25, -137.16) * mm});
            skLineSegment(sketch, "E196.bottom", {"start": v(-196.85, -21.59) * mm, "end": v(-196.85, 130.81) * mm, "construction": true});
            skLineSegment(sketch, "E196.top", {"start": v(31.75, -21.59) * mm, "end": v(31.75, 130.81) * mm, "construction": true});
            skLineSegment(sketch, "E196.left", {"start": v(-190.5, -27.94) * mm, "end": v(25.4, -27.94) * mm, "construction": true});
            skLineSegment(sketch, "E196.right", {"start": v(-190.5, 137.16) * mm, "end": v(25.4, 137.16) * mm, "construction": true});
            skLineSegment(sketch, "E197", {"start": v(142.6, -24.8) * mm, "end": v(186.74, -2.32) * mm, "construction": true});
            skLineSegment(sketch, "E198", {"start": v(142.6, -24.8) * mm, "end": v(155.87, -50.83) * mm});
            skLineSegment(sketch, "E199", {"start": v(164.4, -53.6) * mm, "end": v(177.99, -46.7) * mm});
            skLineSegment(sketch, "E200", {"start": v(177.99, -46.7) * mm, "end": v(190.67, -71.59) * mm});
            skLineSegment(sketch, "E201", {"start": v(190.67, -71.59) * mm, "end": v(195.2, -69.28) * mm});
            skLineSegment(sketch, "E202", {"start": v(160.32, -0.82) * mm, "end": v(180.68, 9.56) * mm});
            skLineSegment(sketch, "E203", {"start": v(180.68, 9.56) * mm, "end": v(186.74, -2.32) * mm});
            skPoint(sketch, "E204.visualSharp", {"position": v(158.75, -56.5) * mm});
            skArc(sketch, "E204.filletArc", {"start": v(155.87, -50.83) * mm, "mid": v(159.56, -54) * mm, "end": v(164.4, -53.6) * mm});
            skArc(sketch, "E205.MirrorCS", {"start": v(129.35, 1.22) * mm, "mid": v(128.96, 6.06) * mm, "end": v(132.12, 9.76) * mm});
            skLineSegment(sketch, "E206.MirrorCS", {"start": v(145.7, 16.68) * mm, "end": v(133.02, 41.57) * mm});
            skLineSegment(sketch, "E207.MirrorCS", {"start": v(132.12, 9.76) * mm, "end": v(145.7, 16.68) * mm});
            skPoint(sketch, "E208.MirrorP", {"position": v(126.46, 6.88) * mm});
            skLineSegment(sketch, "E209.MirrorCS", {"start": v(172.42, -24.58) * mm, "end": v(192.8, -14.2) * mm});
            skLineSegment(sketch, "E210.MirrorCS", {"start": v(142.6, -24.8) * mm, "end": v(129.35, 1.22) * mm});
            skLineSegment(sketch, "E211.MirrorCS", {"start": v(192.8, -14.2) * mm, "end": v(186.74, -2.32) * mm});
            skLineSegment(sketch, "E212", {"start": v(172.42, -24.58) * mm, "end": v(195.2, -69.28) * mm});
            skPoint(sketch, "E213.visualSharp", {"position": v(-222.25, 156.21) * mm});
            skArc(sketch, "E213.filletArc", {"start": v(-203.2, 156.21) * mm, "mid": v(-216.67, 150.63) * mm, "end": v(-222.25, 137.16) * mm});
            skPoint(sketch, "E214.visualSharp", {"position": v(222.25, 156.21) * mm});
            skArc(sketch, "E214.filletArc", {"start": v(222.25, 137.16) * mm, "mid": v(216.67, 150.63) * mm, "end": v(203.2, 156.21) * mm});
            skPoint(sketch, "E215.visualSharp", {"position": v(222.25, -156.2) * mm});
            skArc(sketch, "E215.filletArc", {"start": v(203.2, -156.2) * mm, "mid": v(216.67, -150.63) * mm, "end": v(222.25, -137.16) * mm});
            skPoint(sketch, "E216.visualSharp", {"position": v(-222.25, -156.2) * mm});
            skArc(sketch, "E216.filletArc", {"start": v(-222.25, -137.16) * mm, "mid": v(-216.67, -150.63) * mm, "end": v(-203.2, -156.21) * mm});
            skPoint(sketch, "E217.visualSharp", {"position": v(-196.85, -27.94) * mm});
            skArc(sketch, "E217.filletArc", {"start": v(-196.85, -21.59) * mm, "mid": v(-195, -26.08) * mm, "end": v(-190.5, -27.94) * mm, "construction": true});
            skPoint(sketch, "E218.visualSharp", {"position": v(31.75, -27.94) * mm});
            skArc(sketch, "E218.filletArc", {"start": v(25.4, -27.94) * mm, "mid": v(29.9, -26.08) * mm, "end": v(31.75, -21.59) * mm, "construction": true});
            skPoint(sketch, "E219.visualSharp", {"position": v(-196.85, 137.16) * mm});
            skArc(sketch, "E219.filletArc", {"start": v(-190.5, 137.16) * mm, "mid": v(-195, 135.3) * mm, "end": v(-196.85, 130.81) * mm, "construction": true});
            skPoint(sketch, "E220.visualSharp", {"position": v(31.75, 137.16) * mm});
            skArc(sketch, "E220.filletArc", {"start": v(31.75, 130.81) * mm, "mid": v(29.9, 135.3) * mm, "end": v(25.4, 137.16) * mm, "construction": true});
            skLineSegment(sketch, "E221.bottom", {"start": v(63.5, 88.9) * mm, "end": v(63.5, 124.46) * mm});
            skLineSegment(sketch, "E221.top", {"start": v(196.85, 88.9) * mm, "end": v(196.85, 112.08) * mm});
            skLineSegment(sketch, "E221.left", {"start": v(69.85, 82.55) * mm, "end": v(146.05, 82.55) * mm});
            skLineSegment(sketch, "E221.right", {"start": v(69.85, 130.81) * mm, "end": v(190.5, 130.81) * mm});
            skLineSegment(sketch, "E222.bottom", {"start": v(147.32, 81.28) * mm, "end": v(147.32, 63.5) * mm});
            skLineSegment(sketch, "E222.top", {"start": v(166.37, 81.28) * mm, "end": v(166.37, 63.5) * mm});
            skLineSegment(sketch, "E222.right", {"start": v(153.67, 57.15) * mm, "end": v(160.02, 57.15) * mm});
            skLineSegment(sketch, "E223.trimOffspring", {"start": v(167.64, 82.55) * mm, "end": v(190.5, 82.55) * mm});
            skLineSegment(sketch, "E224", {"start": v(147.32, 82.55) * mm, "end": v(166.37, 82.55) * mm, "construction": true});
            skPoint(sketch, "E225.visualSharp", {"position": v(63.5, 82.55) * mm});
            skArc(sketch, "E225.filletArc", {"start": v(63.5, 88.9) * mm, "mid": v(65.36, 84.4) * mm, "end": v(69.85, 82.55) * mm});
            skPoint(sketch, "E226.visualSharp", {"position": v(196.85, 82.55) * mm});
            skArc(sketch, "E226.filletArc", {"start": v(190.5, 82.55) * mm, "mid": v(195, 84.4) * mm, "end": v(196.85, 88.9) * mm});
            skPoint(sketch, "E227.visualSharp", {"position": v(196.85, 130.81) * mm});
            skArc(sketch, "E227.filletArc", {"start": v(196.85, 124.46) * mm, "mid": v(195, 128.95) * mm, "end": v(190.5, 130.81) * mm});
            skPoint(sketch, "E228.visualSharp", {"position": v(63.5, 130.81) * mm});
            skArc(sketch, "E228.filletArc", {"start": v(69.85, 130.81) * mm, "mid": v(65.36, 128.95) * mm, "end": v(63.5, 124.46) * mm});
            skPoint(sketch, "E229.visualSharp", {"position": v(147.32, 57.15) * mm});
            skArc(sketch, "E229.filletArc", {"start": v(147.32, 63.5) * mm, "mid": v(149.18, 59) * mm, "end": v(153.67, 57.15) * mm});
            skPoint(sketch, "E230.visualSharp", {"position": v(166.37, 57.15) * mm});
            skArc(sketch, "E230.filletArc", {"start": v(160.02, 57.15) * mm, "mid": v(164.51, 59) * mm, "end": v(166.37, 63.5) * mm});
            skLineSegment(sketch, "E231.bottom", {"start": v(127.38, -66.77) * mm, "end": v(150.49, -66.77) * mm, "construction": true});
            skLineSegment(sketch, "E231.left", {"start": v(127.38, -66.77) * mm, "end": v(127.38, -92.17) * mm});
            skLineSegment(sketch, "E231.right", {"start": v(150.49, -66.77) * mm, "end": v(150.49, -92.17) * mm});
            skArc(sketch, "E232", {"start": v(127.38, -92.17) * mm, "mid": v(138.93, -103.73) * mm, "end": v(150.49, -92.17) * mm});
            skLineSegment(sketch, "E233.bottom", {"start": v(-196.85, -139.7) * mm, "end": v(-196.85, -44.45) * mm, "construction": true});
            skLineSegment(sketch, "E233.top", {"start": v(31.75, -139.7) * mm, "end": v(31.75, -44.45) * mm, "construction": true});
            skLineSegment(sketch, "E233.left", {"start": v(-196.85, -139.7) * mm, "end": v(31.75, -139.7) * mm, "construction": true});
            skLineSegment(sketch, "E233.right", {"start": v(-196.85, -44.45) * mm, "end": v(31.75, -44.45) * mm, "construction": true});
            skLineSegment(sketch, "E234", {"start": v(-196.85, -92.07) * mm, "end": v(31.75, -92.07) * mm, "construction": true});
            skLineSegment(sketch, "E235", {"start": v(-196.85, -123.82) * mm, "end": v(31.75, -123.82) * mm, "construction": true});
            skLineSegment(sketch, "E236.MirrorCS", {"start": v(-196.85, -60.32) * mm, "end": v(31.75, -60.32) * mm, "construction": true});
            skLineSegment(sketch, "E237", {"start": v(-196.85, -127.63) * mm, "end": v(31.75, -127.63) * mm, "construction": true});
            skLineSegment(sketch, "E238.MirrorCS", {"start": v(-196.85, -56.51) * mm, "end": v(31.75, -56.51) * mm, "construction": true});
            skLineSegment(sketch, "E239", {"start": v(-177.16, -139.7) * mm, "end": v(-177.16, -44.45) * mm, "construction": true});
            skLineSegment(sketch, "E240", {"start": v(-133.35, -139.7) * mm, "end": v(-133.35, -44.45) * mm, "construction": true});
            skLineSegment(sketch, "E241", {"start": v(-12.7, -139.7) * mm, "end": v(-12.7, -44.45) * mm, "construction": true});
            skLineSegment(sketch, "E242", {"start": v(-196.85, -120.79) * mm, "end": v(-196.85, -63.36) * mm});
            skLineSegment(sketch, "E243", {"start": v(-194.49, -58.42) * mm, "end": v(-178.9, -45.86) * mm});
            skLineSegment(sketch, "E244", {"start": v(-174.92, -44.45) * mm, "end": v(-133.35, -44.45) * mm});
            skLineSegment(sketch, "E245", {"start": v(-133.35, -44.45) * mm, "end": v(-12.7, -56.51) * mm});
            skLineSegment(sketch, "E246", {"start": v(-12.7, -56.51) * mm, "end": v(25.4, -56.51) * mm});
            skLineSegment(sketch, "E247", {"start": v(31.75, -62.86) * mm, "end": v(31.75, -121.28) * mm});
            skLineSegment(sketch, "E248", {"start": v(25.4, -127.63) * mm, "end": v(-12.7, -127.63) * mm});
            skLineSegment(sketch, "E249", {"start": v(-12.7, -127.63) * mm, "end": v(-133.35, -139.7) * mm});
            skLineSegment(sketch, "E250", {"start": v(-133.35, -139.7) * mm, "end": v(-174.92, -139.7) * mm});
            skLineSegment(sketch, "E251", {"start": v(-178.9, -138.3) * mm, "end": v(-194.49, -125.73) * mm});
            skPoint(sketch, "E252.visualSharp", {"position": v(31.75, -127.63) * mm});
            skArc(sketch, "E252.filletArc", {"start": v(25.4, -127.63) * mm, "mid": v(29.9, -125.78) * mm, "end": v(31.75, -121.28) * mm});
            skPoint(sketch, "E253.visualSharp", {"position": v(31.75, -56.51) * mm});
            skArc(sketch, "E253.filletArc", {"start": v(31.75, -62.86) * mm, "mid": v(29.9, -58.37) * mm, "end": v(25.4, -56.51) * mm});
            skPoint(sketch, "E254.visualSharp", {"position": v(-196.85, -123.82) * mm});
            skArc(sketch, "E254.filletArc", {"start": v(-196.85, -120.79) * mm, "mid": v(-196.23, -123.53) * mm, "end": v(-194.49, -125.73) * mm});
            skPoint(sketch, "E255.visualSharp", {"position": v(-177.16, -139.7) * mm});
            skArc(sketch, "E255.filletArc", {"start": v(-178.9, -138.3) * mm, "mid": v(-177.04, -139.34) * mm, "end": v(-174.92, -139.7) * mm});
            skPoint(sketch, "E256.visualSharp", {"position": v(-196.85, -60.32) * mm});
            skArc(sketch, "E256.filletArc", {"start": v(-194.49, -58.42) * mm, "mid": v(-196.23, -60.62) * mm, "end": v(-196.85, -63.36) * mm});
            skPoint(sketch, "E257.visualSharp", {"position": v(-177.16, -44.45) * mm});
            skArc(sketch, "E257.filletArc", {"start": v(-174.92, -44.45) * mm, "mid": v(-177.04, -44.81) * mm, "end": v(-178.9, -45.86) * mm});
            skLineSegment(sketch, "E258", {"start": v(127.38, -92.17) * mm, "end": v(150.49, -92.17) * mm, "construction": true});
            skLineSegment(sketch, "E259.MirrorCS", {"start": v(160.32, -0.82) * mm, "end": v(137.54, 43.88) * mm});
            skLineSegment(sketch, "E260.MirrorCS", {"start": v(133.02, 41.57) * mm, "end": v(137.54, 43.88) * mm});
            skLineSegment(sketch, "E261", {"start": v(198.12, 122.87) * mm, "end": v(198.76, 122.87) * mm});
            skLineSegment(sketch, "E262", {"start": v(200.03, 121.6) * mm, "end": v(200.03, 114.62) * mm});
            skLineSegment(sketch, "E263", {"start": v(198.76, 113.35) * mm, "end": v(198.12, 113.35) * mm});
            skPoint(sketch, "E264.visualSharp", {"position": v(166.37, 82.55) * mm});
            skArc(sketch, "E264.filletArc", {"start": v(167.64, 82.55) * mm, "mid": v(166.74, 82.18) * mm, "end": v(166.37, 81.28) * mm});
            skPoint(sketch, "E265.visualSharp", {"position": v(147.32, 82.55) * mm});
            skArc(sketch, "E265.filletArc", {"start": v(147.32, 81.28) * mm, "mid": v(146.95, 82.18) * mm, "end": v(146.05, 82.55) * mm});
            skPoint(sketch, "E266.visualSharp", {"position": v(200.03, 113.35) * mm});
            skArc(sketch, "E266.filletArc", {"start": v(198.76, 113.35) * mm, "mid": v(199.65, 113.72) * mm, "end": v(200.03, 114.62) * mm});
            skPoint(sketch, "E267.visualSharp", {"position": v(200.03, 122.87) * mm});
            skArc(sketch, "E267.filletArc", {"start": v(200.03, 121.6) * mm, "mid": v(199.65, 122.5) * mm, "end": v(198.76, 122.87) * mm});
            skPoint(sketch, "E268.visualSharp", {"position": v(196.85, 122.87) * mm});
            skArc(sketch, "E268.filletArc", {"start": v(196.85, 124.13) * mm, "mid": v(197.23, 123.24) * mm, "end": v(198.12, 122.87) * mm});
            skPoint(sketch, "E269.visualSharp", {"position": v(196.85, 113.35) * mm});
            skArc(sketch, "E269.filletArc", {"start": v(198.12, 113.35) * mm, "mid": v(197.22, 112.98) * mm, "end": v(196.85, 112.08) * mm});
            skLineSegment(sketch, "E270", {"start": v(-196.85, 54.61) * mm, "end": v(31.75, 54.61) * mm, "construction": true});
            skLineSegment(sketch, "E271", {"start": v(-82.55, -27.94) * mm, "end": v(-82.55, 137.16) * mm, "construction": true});
            skLineSegment(sketch, "E272", {"start": v(0, 156.21) * mm, "end": v(0, -156.2) * mm, "construction": true});
            skLineSegment(sketch, "E273", {"start": v(-222.25, 0) * mm, "end": v(222.25, 0) * mm, "construction": true});
            skPoint(sketch, "E274", {"position": v(0, 0) * mm});
            skPoint(sketch, "E275", {"position": v(-82.55, 54.61) * mm});
            skPoint(sketch, "E276", {"position": v(-133.35, -92.07) * mm});
            skLineSegment(sketch, "E277", {"start": v(63.5, 106.68) * mm, "end": v(196.85, 106.68) * mm, "construction": true});
            skLineSegment(sketch, "E278", {"start": v(130.18, 130.81) * mm, "end": v(130.18, 82.55) * mm, "construction": true});
            skPoint(sketch, "E279", {"position": v(130.18, 106.68) * mm});
            skLineSegment(sketch, "E280", {"start": v(172.42, -24.58) * mm, "end": v(160.32, -0.82) * mm, "construction": true});
            skPoint(sketch, "E281", {"position": v(166.37, -12.7) * mm});
            skLineSegment(sketch, "E282", {"start": v(196.85, 124.46) * mm, "end": v(196.85, 124.13) * mm});
            skLineSegment(sketch, "E283", {"start": v(196.85, 124.13) * mm, "end": v(196.85, 112.08) * mm, "construction": true});
            skArc(sketch, "E284", {"start": v(31.75, -21.59) * mm, "mid": v(29.9, -26.08) * mm, "end": v(25.4, -27.94) * mm, "construction": true});
            skLineSegment(sketch, "E285.bottom", {"start": v(107.95, -137.16) * mm, "end": v(57.15, -137.16) * mm});
            skLineSegment(sketch, "E285.top", {"start": v(107.95, 66.04) * mm, "end": v(57.15, 66.04) * mm});
            skLineSegment(sketch, "E285.left", {"start": v(114.3, -130.8) * mm, "end": v(114.3, 59.69) * mm});
            skLineSegment(sketch, "E285.right", {"start": v(50.8, -130.8) * mm, "end": v(50.8, 59.69) * mm});
            skLineSegment(sketch, "E286", {"start": v(82.55, -137.16) * mm, "end": v(82.55, 66.04) * mm, "construction": true});
            skLineSegment(sketch, "E287", {"start": v(114.3, -35.56) * mm, "end": v(50.8, -35.56) * mm, "construction": true});
            skPoint(sketch, "E288", {"position": v(82.55, -35.56) * mm});
            skPoint(sketch, "E289.visualSharp", {"position": v(114.3, -137.16) * mm});
            skArc(sketch, "E289.filletArc", {"start": v(107.95, -137.16) * mm, "mid": v(112.44, -135.3) * mm, "end": v(114.3, -130.8) * mm});
            skPoint(sketch, "E290.visualSharp", {"position": v(50.8, -137.16) * mm});
            skArc(sketch, "E290.filletArc", {"start": v(50.8, -130.8) * mm, "mid": v(52.66, -135.3) * mm, "end": v(57.15, -137.16) * mm});
            skPoint(sketch, "E291.visualSharp", {"position": v(50.8, 66.04) * mm});
            skArc(sketch, "E291.filletArc", {"start": v(57.15, 66.04) * mm, "mid": v(52.66, 64.18) * mm, "end": v(50.8, 59.69) * mm});
            skPoint(sketch, "E292.visualSharp", {"position": v(114.3, 66.04) * mm});
            skArc(sketch, "E292.filletArc", {"start": v(114.3, 59.69) * mm, "mid": v(112.44, 64.18) * mm, "end": v(107.95, 66.04) * mm});
            skLineSegment(sketch, "E293.bottom", {"start": v(-193.68, 143.5) * mm, "end": v(28.58, 143.5) * mm});
            skLineSegment(sketch, "E293.top", {"start": v(-193.68, -34.3) * mm, "end": v(0, -34.3) * mm});
            skLineSegment(sketch, "E293.left", {"start": v(-206.38, 130.8) * mm, "end": v(-206.38, 111.76) * mm});
            skLineSegment(sketch, "E293.right", {"start": v(41.28, 130.8) * mm, "end": v(41.27, -21.6) * mm});
            skPoint(sketch, "E294.visualSharp", {"position": v(-206.38, 143.5) * mm});
            skArc(sketch, "E294.filletArc", {"start": v(-193.68, 143.5) * mm, "mid": v(-202.66, 139.8) * mm, "end": v(-206.38, 130.8) * mm});
            skPoint(sketch, "E295.visualSharp", {"position": v(41.28, 143.5) * mm});
            skArc(sketch, "E295.filletArc", {"start": v(41.28, 130.8) * mm, "mid": v(37.56, 139.8) * mm, "end": v(28.58, 143.51) * mm});
            skPoint(sketch, "E296.visualSharp", {"position": v(41.27, -34.3) * mm});
            skArc(sketch, "E296.filletArc", {"start": v(28.57, -34.3) * mm, "mid": v(37.56, -30.57) * mm, "end": v(41.27, -21.6) * mm});
            skPoint(sketch, "E297.visualSharp", {"position": v(-206.38, -34.3) * mm});
            skArc(sketch, "E297.filletArc", {"start": v(-206.38, -21.6) * mm, "mid": v(-202.66, -30.57) * mm, "end": v(-193.68, -34.3) * mm});
            skArc(sketch, "E298", {"start": v(-206.38, 62.23) * mm, "mid": v(-214, 54.6) * mm, "end": v(-206.38, 46.99) * mm});
            skLineSegment(sketch, "E299", {"start": v(-206.38, 62.23) * mm, "end": v(-206.38, 46.99) * mm, "construction": true});
            skLineSegment(sketch, "E300", {"start": v(-206.38, 46.99) * mm, "end": v(-206.38, -21.6) * mm});
            skLineSegment(sketch, "E301", {"start": v(-193.68, 111.76) * mm, "end": v(0, 111.76) * mm});
            skLineSegment(sketch, "E302", {"start": v(12.7, 99.06) * mm, "end": v(12.7, -21.6) * mm});
            skPoint(sketch, "E303.visualSharp", {"position": v(12.7, 111.76) * mm});
            skArc(sketch, "E303.filletArc", {"start": v(12.7, 99.06) * mm, "mid": v(8.98, 108.04) * mm, "end": v(0, 111.76) * mm});
            skLineSegment(sketch, "E304", {"start": v(-206.38, 99.06) * mm, "end": v(-206.38, 62.23) * mm});
            skLineSegment(sketch, "E305", {"start": v(12.7, -34.3) * mm, "end": v(28.57, -34.3) * mm});
            skPoint(sketch, "E306.visualSharp", {"position": v(-206.38, 111.76) * mm});
            skArc(sketch, "E306.filletArc", {"start": v(-193.68, 111.76) * mm, "mid": v(-202.66, 108.04) * mm, "end": v(-206.38, 99.06) * mm});
            skPoint(sketch, "E307.visualSharp", {"position": v(12.7, -34.29) * mm});
            skArc(sketch, "E307.filletArc", {"start": v(0, -34.3) * mm, "mid": v(8.98, -30.57) * mm, "end": v(12.7, -21.6) * mm});
            skLineSegment(sketch, "E308", {"start": v(-206.38, 111.76) * mm, "end": v(-206.38, 99.06) * mm});
            skLineSegment(sketch, "E309", {"start": v(12.7, -34.3) * mm, "end": v(0, -34.3) * mm});
            skLineSegment(sketch, "E310.0.0", {"start": v(171.94, 54.19) * mm, "end": v(171.94, 23.7) * mm});
            skLineSegment(sketch, "E310.0.1", {"start": v(171.94, 23.7) * mm, "end": v(202.42, 23.7) * mm});
            skLineSegment(sketch, "E310.0.2", {"start": v(202.42, 23.7) * mm, "end": v(202.42, 54.19) * mm});
            skLineSegment(sketch, "E310.0.3", {"start": v(202.42, 54.19) * mm, "end": v(171.94, 54.19) * mm});
            skArc(sketch, "E311", {"start": v(127.38, -66.77) * mm, "mid": v(138.93, -55.22) * mm, "end": v(150.49, -66.77) * mm});
            skPoint(sketch, "E312.first.point", {"position": v(168.37, -99.62) * mm});
            skPoint(sketch, "E312.second.point", {"position": v(206.77, -114.22) * mm});
            skCircle(sketch, "E313", {"center": v(192.42, -105.78) * mm, "radius": 3.63 * mm});
            skPoint(sketch, "E313.first.point", {"position": v(189.24, -104.04) * mm});
            skPoint(sketch, "E313.second.point", {"position": v(194.51, -102.83) * mm});
            skPoint(sketch, "E313.third.point", {"position": v(192.87, -109.38) * mm});
            skPoint(sketch, "E314.first.point", {"position": v(187.18, -101.37) * mm});
            skPoint(sketch, "E314.second.point", {"position": v(197.46, -101.18) * mm});
            skPoint(sketch, "E314.third.point", {"position": v(196.72, -111.02) * mm});
            skLineSegment(sketch, "E315", {"start": v(165.87, -102.3) * mm, "end": v(186.53, -102.3) * mm});
            skLineSegment(sketch, "E316", {"start": v(162.1, -109.2) * mm, "end": v(186.52, -109.2) * mm});
            skLineSegment(sketch, "E317", {"start": v(189.01, -139.07) * mm, "end": v(189.01, -139.07) * mm});
            skLineSegment(sketch, "E318", {"start": v(195.96, -136.23) * mm, "end": v(195.96, -111.56) * mm});
            skLineSegment(sketch, "E319", {"start": v(201.88, -102.3) * mm, "end": v(201.88, -102.3) * mm});
            skLineSegment(sketch, "E320", {"start": v(205.66, -109.2) * mm, "end": v(205.66, -109.2) * mm});
            skArc(sketch, "E321", {"start": v(201.88, -102.3) * mm, "mid": v(199.15, -99.4) * mm, "end": v(195.96, -97.04) * mm});
            skLineSegment(sketch, "E322", {"start": v(198.27, -102.3) * mm, "end": v(201.88, -102.3) * mm});
            skLineSegment(sketch, "E323", {"start": v(195.96, -99.94) * mm, "end": v(195.96, -97.04) * mm});
            skArc(sketch, "E324", {"start": v(198.27, -102.3) * mm, "mid": v(197.26, -100.97) * mm, "end": v(195.96, -99.94) * mm});
            skArc(sketch, "E325", {"start": v(195.96, -111.56) * mm, "mid": v(197.27, -110.52) * mm, "end": v(198.28, -109.2) * mm});
            skArc(sketch, "E326", {"start": v(186.52, -109.2) * mm, "mid": v(187.6, -110.59) * mm, "end": v(189.01, -111.66) * mm});
            skArc(sketch, "E327", {"start": v(189.01, -99.84) * mm, "mid": v(187.6, -100.9) * mm, "end": v(186.53, -102.3) * mm});
            skLineSegment(sketch, "E328", {"start": v(189.01, -99.84) * mm, "end": v(189.01, -94.2) * mm});
            skLineSegment(sketch, "E329", {"start": v(188.99, -111.65) * mm, "end": v(188.99, -111.65) * mm});
            skLineSegment(sketch, "E330", {"start": v(198.28, -109.2) * mm, "end": v(198.28, -109.2) * mm});
            skLineSegment(sketch, "E331", {"start": v(198.28, -109.2) * mm, "end": v(205.66, -109.2) * mm});
            skLineSegment(sketch, "E332", {"start": v(189.01, -94.2) * mm, "end": v(189.01, -94.2) * mm});
            skArc(sketch, "E333", {"start": v(189.01, -94.2) * mm, "mid": v(176.27, -94.9) * mm, "end": v(165.87, -102.3) * mm});
            skArc(sketch, "E334", {"start": v(162.1, -109.2) * mm, "mid": v(166.77, -132.04) * mm, "end": v(189.01, -139.07) * mm});
            skLineSegment(sketch, "E335", {"start": v(189.01, -139.07) * mm, "end": v(189.01, -111.66) * mm});
            skArc(sketch, "E336", {"start": v(195.96, -136.23) * mm, "mid": v(205.54, -124.4) * mm, "end": v(205.66, -109.2) * mm});
            skSolve(sketch);
        }
        {
            var Q0;
            Q0=qSketchRegion(id+"F4",true);
            extrude(context, id + "F5", {"entities" : qUnion([Q0]), "depth" : 12.7 * mm, "offsetDistance" : 25.4 * mm});
        }
    });
